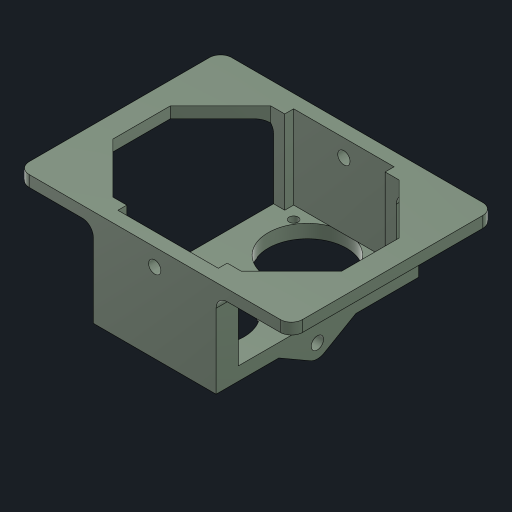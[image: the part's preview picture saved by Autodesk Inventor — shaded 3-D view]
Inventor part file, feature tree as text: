
AUTODESK INVENTOR PART (.ipt)
format: ipt  version: 2023 (Build 270158000, 158)  size: 361,984 bytes
history: native  units: mm
features: sketch x9, extrude x8, fillet x3, projected_geometry x3, hole x2, mirror x2, other x1, chamfer x1
ambient origin geometry x8: Origin, YZ Plane, XZ Plane, XY Plane, X Axis, Y Axis, Z Axis, Center Point
bodies: Body1 (feature_tree)
feature tree (29):
  other  "ソリッド1"
  extrude  "押し出し1"  Depth=31.5mm
  sketch  "スケッチ2"
  extrude  "押し出し2"  Depth=22.0mm
  extrude  "押し出し3"  Depth=14.0mm
  extrude  "押し出し5"  Depth=2.4mm TaperAngle=0.0deg
  hole  "穴1"  [1 undecoded]
  extrude  "補強"  Depth=8.5mm
  mirror  "ミラー2"
  extrude  "穴抜き"  Depth=2.0mm
  chamfer  "面取り1"  Distance=49.0mm
  fillet  "フィレット1"  Radius=2.0mm
  hole  "穴2"  [1 undecoded]
  extrude  "押し出し10"  Depth=1.6mm
  fillet  "フィレット2"  Radius=14.0mm
  extrude  "押し出し12"  Depth=9.2mm
  mirror  "ミラー4"
  fillet  "フィレット3"  [1 undecoded]
  sketch  "スケッチ1"
  projected_geometry  "投影ループ1"
  sketch  "スケッチ3"
  sketch  "スケッチ5"
  sketch  "スケッチ6"
  sketch  "スケッチ7"
  sketch  "スケッチ10"
  sketch  "スケッチ11"
  projected_geometry  "投影ループ2"
  projected_geometry  "投影ループ3"
  sketch  "スケッチ13"
note: 3 required parameter values undecoded (feature->parameter linkage not recoverable at this tier; creation-order binding heuristic only, values carry confidence <= 0.55)
